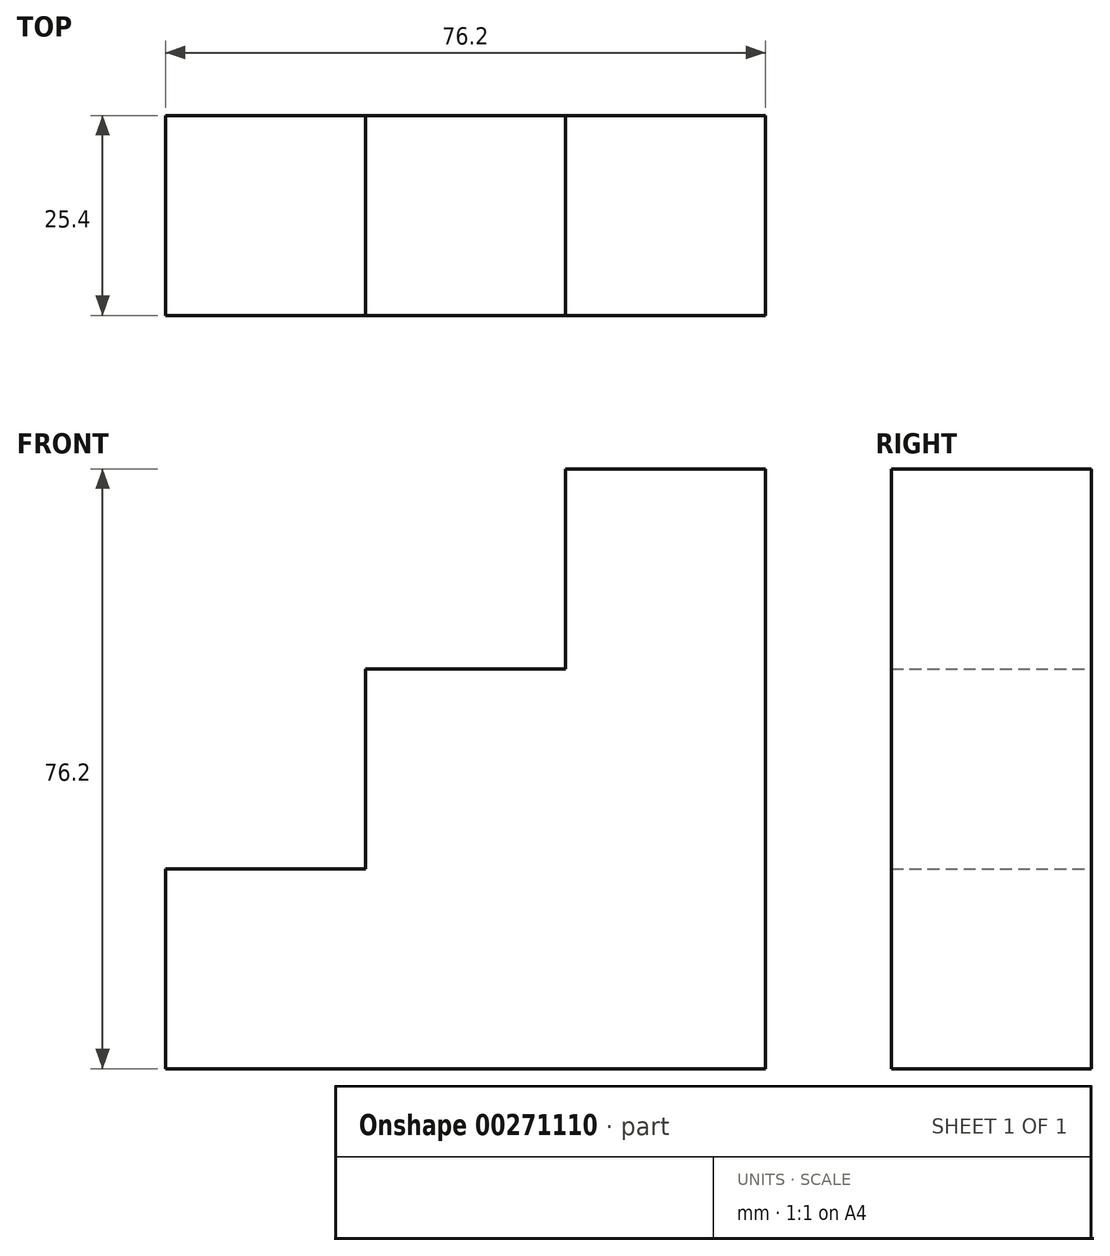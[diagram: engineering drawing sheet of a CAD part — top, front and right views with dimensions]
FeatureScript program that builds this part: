
annotation { "Feature Type Name" : "Feature", "Feature Type Description" : "" }
export const myFeature = defineFeature(function(context is Context, id is Id, definition is map)
    precondition{}
    {
        {
            var Q0;
            Q0=qCreatedBy(makeId("Front.planeOp"),FACE);
            var sketch = newSketch(context, id + "F0", { "sketchPlane" : qUnion([Q0])});
            skLineSegment(sketch, "E0", {"start": v(0, 0) * mm, "end": v(-76.2, 0) * mm});
            skLineSegment(sketch, "E1", {"start": v(0, 0) * mm, "end": v(0, 76.2) * mm});
            skLineSegment(sketch, "E2", {"start": v(0, 76.2) * mm, "end": v(-25.4, 76.2) * mm});
            skLineSegment(sketch, "E3", {"start": v(-25.4, 76.2) * mm, "end": v(-25.4, 50.8) * mm});
            skLineSegment(sketch, "E4", {"start": v(-25.4, 50.8) * mm, "end": v(-50.8, 50.8) * mm});
            skLineSegment(sketch, "E5", {"start": v(-50.8, 50.8) * mm, "end": v(-50.8, 25.4) * mm});
            skLineSegment(sketch, "E6", {"start": v(-50.8, 25.4) * mm, "end": v(-76.2, 25.4) * mm});
            skLineSegment(sketch, "E7", {"start": v(-76.2, 25.4) * mm, "end": v(-76.2, 0) * mm});
            skSolve(sketch);
        }
        {
            var Q0;
            Q0=makeQuery(id+"F0.imprint","IMPRINT",FACE,{"disambiguationData":[TD([[makeQuery(id+"F0.imprint","IMPRINT",EDGE,{"derivedFrom":sQuery(id+"F0.wireOp",EDGE,"E0")}),-1.0]])]});
            extrude(context, id + "F1", {"entities" : qUnion([Q0]), "depth" : 25.4 * mm});
        }
    });
